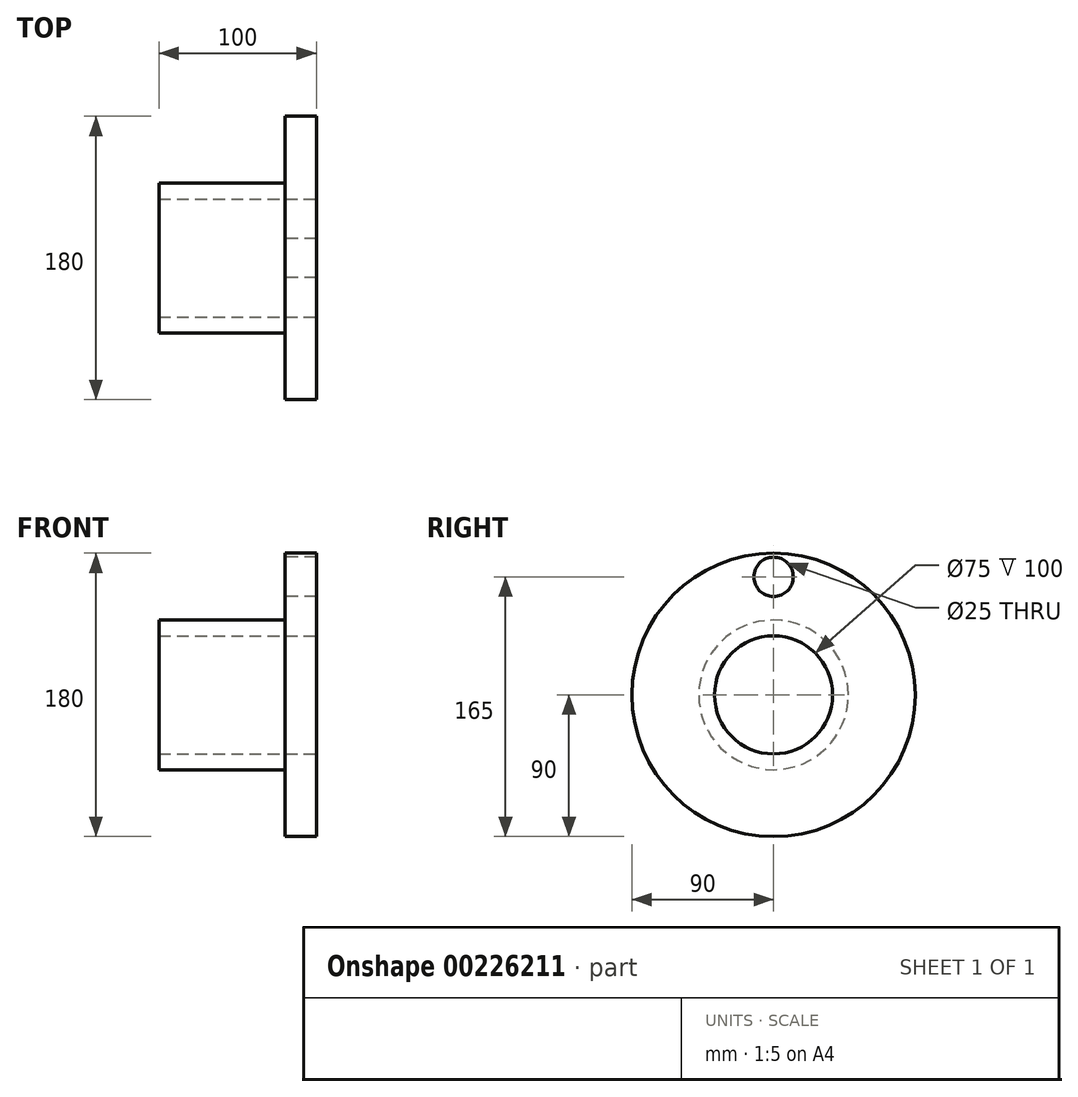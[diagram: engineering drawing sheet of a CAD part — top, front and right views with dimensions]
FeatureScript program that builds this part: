
annotation { "Feature Type Name" : "Feature", "Feature Type Description" : "" }
export const myFeature = defineFeature(function(context is Context, id is Id, definition is map)
    precondition{}
    {
        {
            var Q0;
            Q0=qCreatedBy(makeId("Front.planeOp"),FACE);
            var sketch = newSketch(context, id + "F0", { "sketchPlane" : qUnion([Q0])});
            skLineSegment(sketch, "E0", {"start": v(0, 0) * mm, "end": v(-172.68, 0) * mm, "construction": true});
            skLineSegment(sketch, "E1", {"start": v(0, 37.5) * mm, "end": v(0, 90) * mm});
            skLineSegment(sketch, "E2", {"start": v(0, 90) * mm, "end": v(-20, 90) * mm});
            skLineSegment(sketch, "E3", {"start": v(-20, 90) * mm, "end": v(-20, 47.5) * mm});
            skLineSegment(sketch, "E4", {"start": v(-20, 47.5) * mm, "end": v(-100, 47.5) * mm});
            skLineSegment(sketch, "E5", {"start": v(-100, 47.5) * mm, "end": v(-100, 37.5) * mm});
            skLineSegment(sketch, "E6", {"start": v(-100, 37.5) * mm, "end": v(0, 37.5) * mm});
            skSolve(sketch);
        }
        {
            var Q0;
            Q0 = qSketchRegion(id + "F0", true);
            var Q1;
            Q1=sQuery(id+"F0.wireOp",EDGE,"E0");
            revolve(context, id + "F1", {"entities" : qUnion([Q0]), "axis" : qUnion([Q1]), "revolveType" : RevolveType.FULL});
        }
        {
            var Q0;
            Q0=makeQuery(id+"F1.opRevolve","SWEPT_FACE",FACE,{"disambiguationData":[OSD([sQuery(id+"F0.wireOp",EDGE,"E3")])]});
            var sketch = newSketch(context, id + "F2", { "sketchPlane" : qUnion([Q0])});
            skCircle(sketch, "E7", {"center": v(0, 75) * mm, "radius": 12.5 * mm});
            skSolve(sketch);
        }
        {
            var Q0;
            Q0=makeQuery(id+"F2.imprint","IMPRINT",FACE,{"disambiguationData":[TD([[makeQuery(id+"F2.imprint","IMPRINT",EDGE,{"derivedFrom":sQuery(id+"F2.wireOp",EDGE,"E7")}),1.0]])]});
            extrude(context, id + "F3", {"entities" : qUnion([Q0]), "operationType" : NewBodyOperationType.REMOVE, "endBound" : BoundingType.THROUGH_ALL, "oppositeDirection" : true, "depth" : 25 * mm});
        }
    });
